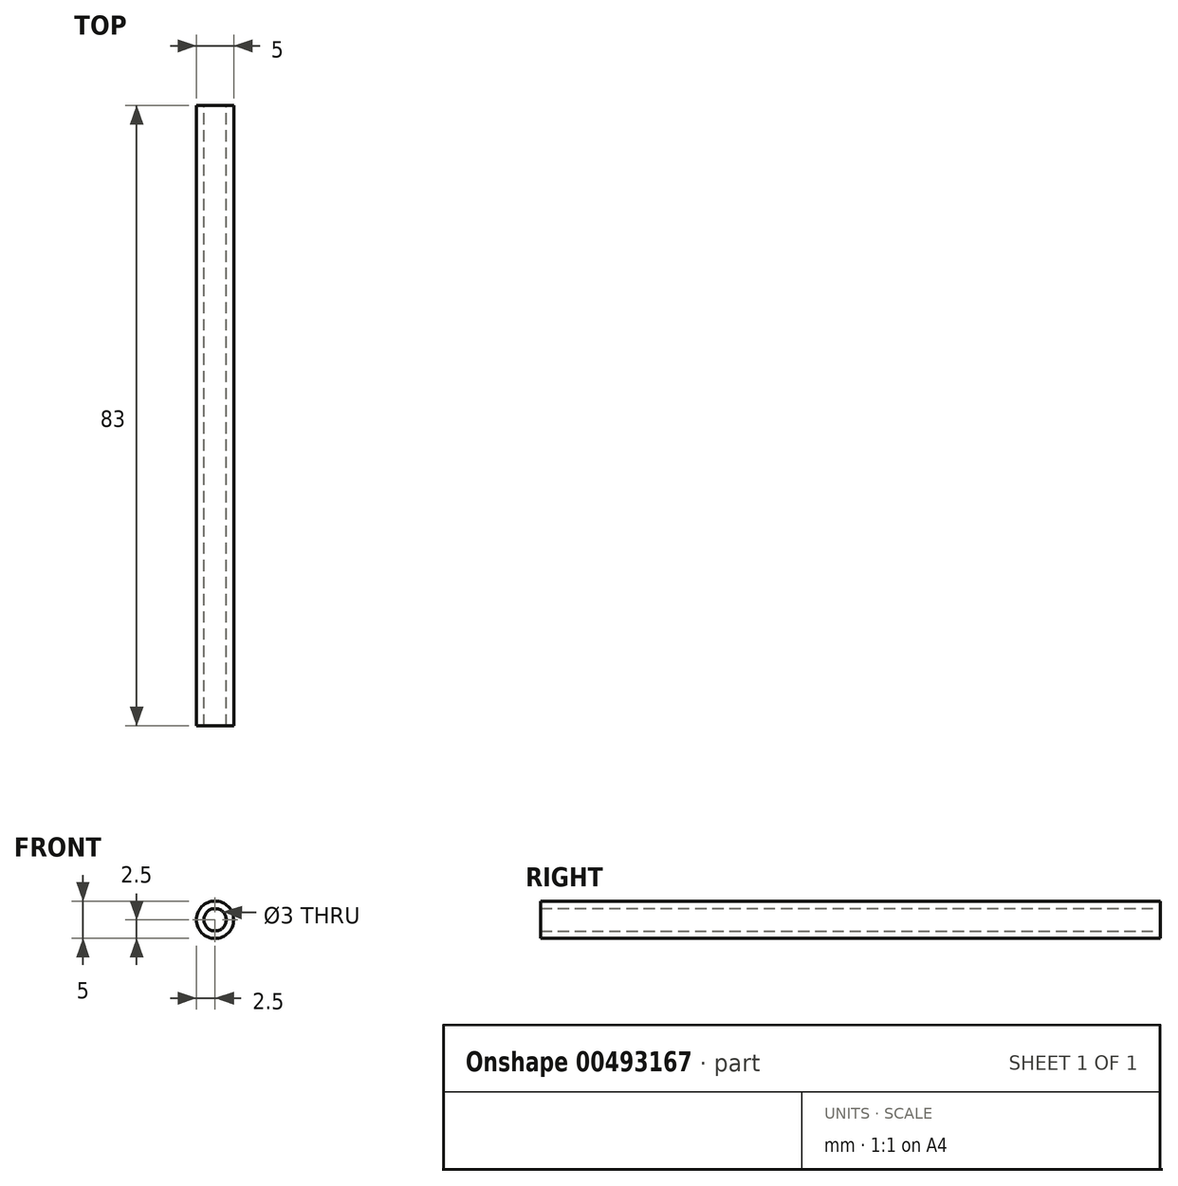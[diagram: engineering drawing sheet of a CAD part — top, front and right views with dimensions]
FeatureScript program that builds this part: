
annotation { "Feature Type Name" : "Feature", "Feature Type Description" : "" }
export const myFeature = defineFeature(function(context is Context, id is Id, definition is map)
    precondition{}
    {
        {
            var Q0;
            Q0=qCreatedBy(makeId("Front.planeOp"),FACE);
            var sketch = newSketch(context, id + "F0", { "sketchPlane" : qUnion([Q0])});
            skCircle(sketch, "E0", {"center": v(0, 0) * mm, "radius": 2.5 * mm});
            skSolve(sketch);
        }
        {
            var Q0;
            Q0 = qSketchRegion(id + "F0", true);
            extrude(context, id + "F1", {"entities" : qUnion([Q0]), "depth" : (87 - 4) * mm});
        }
        {
            var Q0;
            Q0=makeQuery(id+"F1.opExtrude","CAP_FACE",FACE,{"disambiguationData":[OSD([sQuery(id+"F0.wireOp",EDGE,"E0")])],"isStart":true});
            var sketch = newSketch(context, id + "F2", { "sketchPlane" : qUnion([Q0])});
            skCircle(sketch, "E1", {"center": v(0, 0) * mm, "radius": 1.5 * mm});
            skSolve(sketch);
        }
        {
            var Q0;
            Q0 = qSketchRegion(id + "F2", true);
            extrude(context, id + "F3", {"entities" : qUnion([Q0]), "operationType" : NewBodyOperationType.REMOVE, "oppositeDirection" : true, "depth" : 200 * mm});
        }
    });
